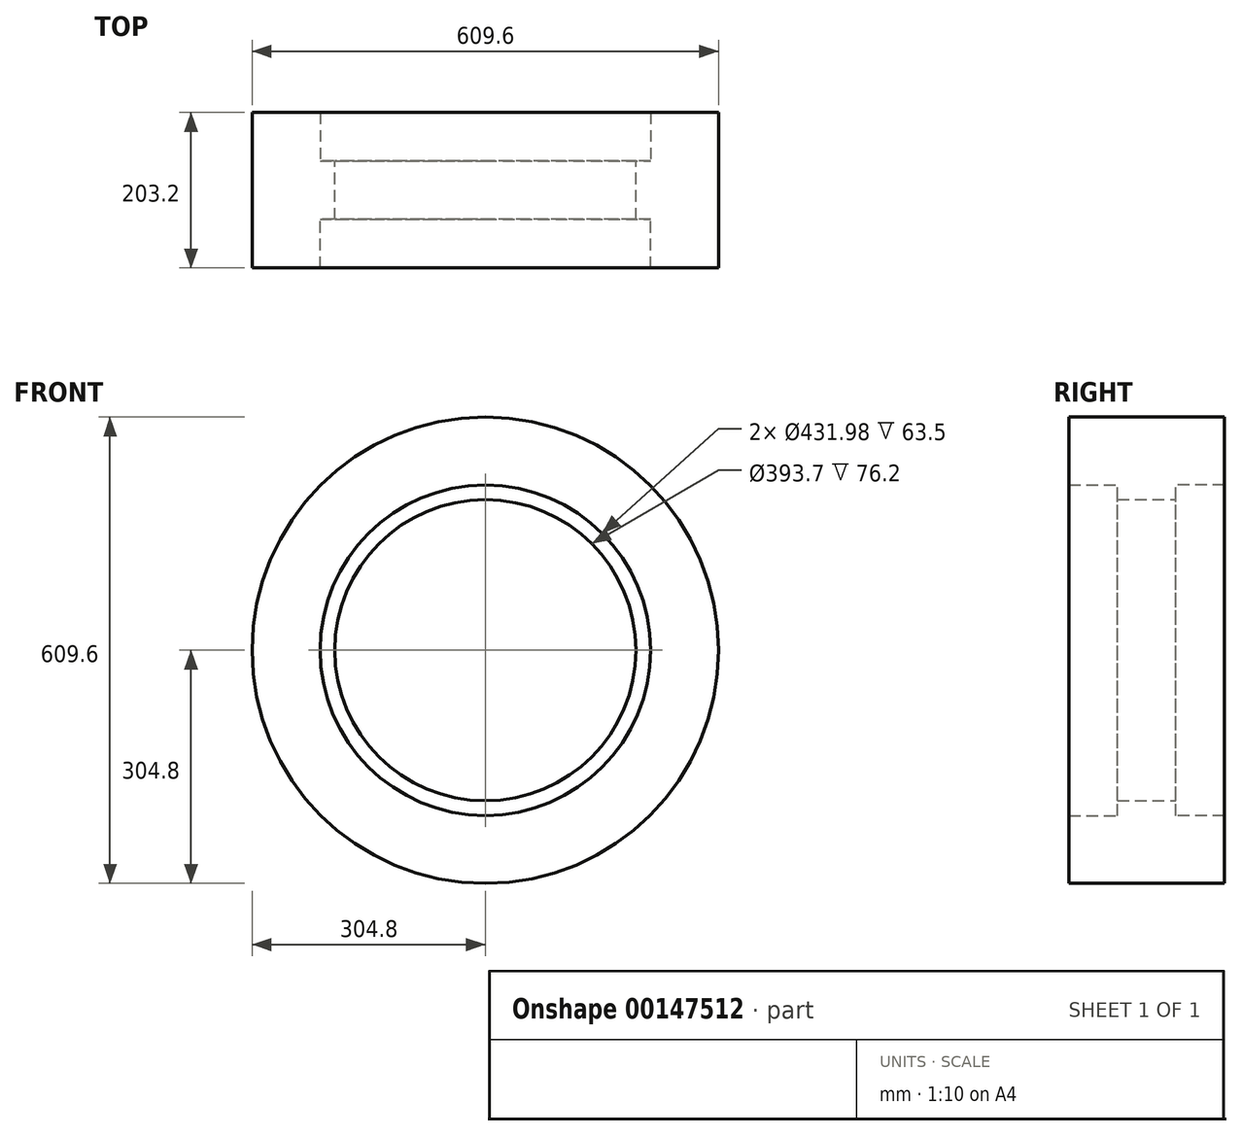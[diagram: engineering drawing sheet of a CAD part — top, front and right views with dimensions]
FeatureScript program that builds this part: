
annotation { "Feature Type Name" : "Feature", "Feature Type Description" : "" }
export const myFeature = defineFeature(function(context is Context, id is Id, definition is map)
    precondition{}
    {
        {
            var Q0;
            Q0=qCreatedBy(makeId("Front.planeOp"),FACE);
            var sketch = newSketch(context, id + "F0", { "sketchPlane" : qUnion([Q0])});
            skCircle(sketch, "E0", {"center": v(0, 0) * mm, "radius": 196.85 * mm});
            skCircle(sketch, "E1", {"center": v(0, 0) * mm, "radius": 304.8 * mm});
            skSolve(sketch);
        }
        {
            var Q0;
            Q0=makeQuery(id+"F0.imprint","IMPRINT",FACE,{"disambiguationData":[TD([[makeQuery(id+"F0.imprint","IMPRINT",EDGE,{"derivedFrom":sQuery(id+"F0.wireOp",EDGE,"E0")}),-1.0]])]});
            extrude(context, id + "F1", {"entities" : qUnion([Q0]), "depth" : 38.1 * mm});
        }
        {
            var Q0;
            Q0=makeQuery(id+"F1.opExtrude","CAP_FACE",FACE,{"disambiguationData":[OSD([sQuery(id+"F0.wireOp",EDGE,"E0"),sQuery(id+"F0.wireOp",EDGE,"E1")])],"isStart":false});
            var sketch = newSketch(context, id + "F2", { "sketchPlane" : qUnion([Q0])});
            skCircle(sketch, "E2", {"center": v(0, 0) * mm, "radius": 215.99 * mm});
            skCircle(sketch, "E3", {"center": v(0, 0) * mm, "radius": 304.8 * mm});
            skSolve(sketch);
        }
        {
            var Q0;
            Q0=makeQuery(id+"F2.imprint","IMPRINT",FACE,{"disambiguationData":[TD([[makeQuery(id+"F2.imprint","IMPRINT",EDGE,{"derivedFrom":sQuery(id+"F2.wireOp",EDGE,"E2")}),-1.0]])]});
            extrude(context, id + "F3", {"entities" : qUnion([Q0]), "operationType" : NewBodyOperationType.ADD, "depth" : 63.5 * mm});
        }
        {
            var Q0;
            Q0=makeQuery(id+"F1.opExtrude","SWEPT_BODY",BODY,{"disambiguationData":[OSD([sQuery(id+"F0.wireOp",EDGE,"E0"),sQuery(id+"F0.wireOp",EDGE,"E1")])]});
            var Q1;
            Q1=makeQuery(id+"F1.opExtrude","CAP_FACE",FACE,{"disambiguationData":[OSD([sQuery(id+"F0.wireOp",EDGE,"E0"),sQuery(id+"F0.wireOp",EDGE,"E1")])],"isStart":true});
            mirror(context, id + "F4", {"operationType" : NewBodyOperationType.ADD, "entities" : qUnion([Q0]), "mirrorPlane" : qUnion([Q1])});
        }
    });
